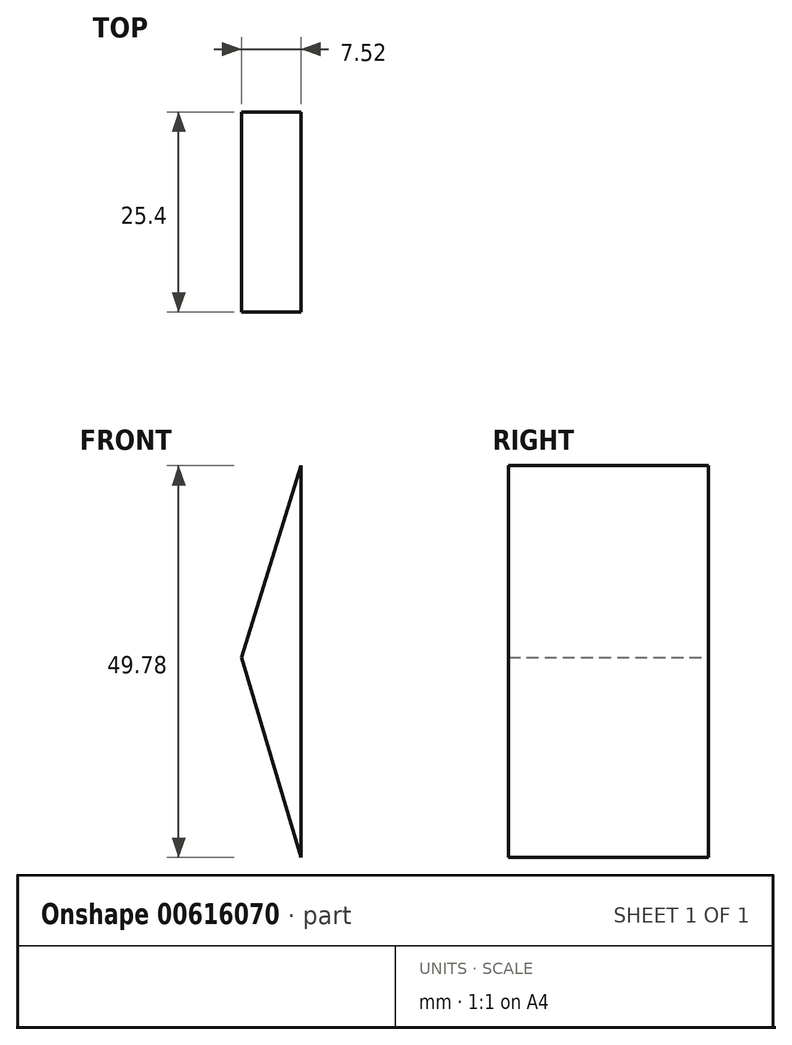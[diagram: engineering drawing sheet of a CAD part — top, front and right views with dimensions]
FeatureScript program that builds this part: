
annotation { "Feature Type Name" : "Feature", "Feature Type Description" : "" }
export const myFeature = defineFeature(function(context is Context, id is Id, definition is map)
    precondition{}
    {
        {
            var Q0;
            Q0=qCreatedBy(makeId("Front.planeOp"),FACE);
            var sketch = newSketch(context, id + "F0", { "sketchPlane" : qUnion([Q0])});
            skLineSegment(sketch, "E0", {"start": v(-44.07, 0) * mm, "end": v(-44.07, 49.78) * mm});
            skLineSegment(sketch, "E1", {"start": v(-44.07, 49.78) * mm, "end": v(-51.59, 25.42) * mm});
            skLineSegment(sketch, "E2", {"start": v(-51.59, 25.42) * mm, "end": v(-44.07, 0) * mm});
            skSolve(sketch);
        }
        {
            var Q0;
            Q0 = qSketchRegion(id + "F0", true);
            extrude(context, id + "F1", {"entities" : qUnion([Q0]), "depth" : 25.4 * mm, "offsetDistance" : 25.4 * mm});
        }
    });
